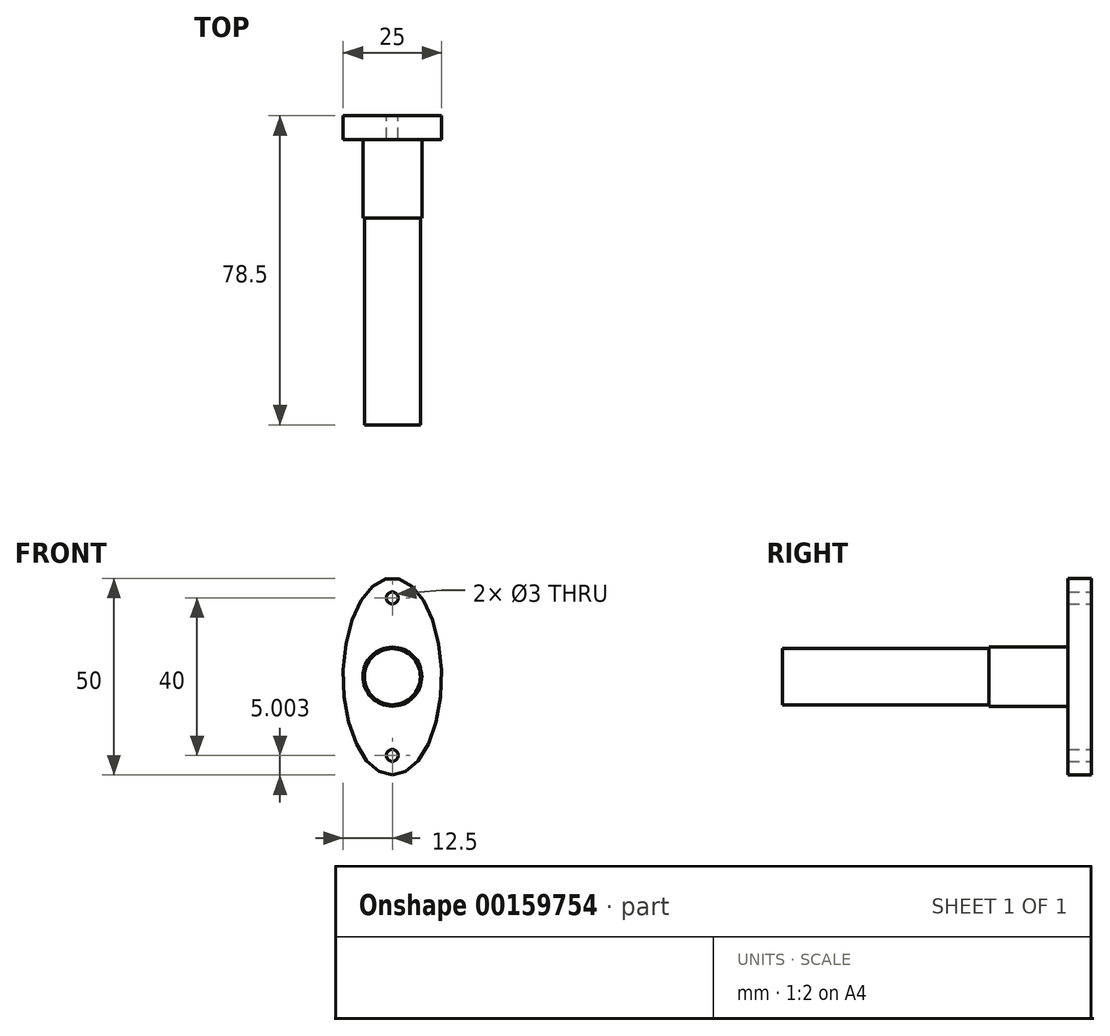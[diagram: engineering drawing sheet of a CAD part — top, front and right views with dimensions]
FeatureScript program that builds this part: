
annotation { "Feature Type Name" : "Feature", "Feature Type Description" : "" }
export const myFeature = defineFeature(function(context is Context, id is Id, definition is map)
    precondition{}
    {
        {
            var Q0;
            Q0=qCreatedBy(makeId("Front.planeOp"),FACE);
            var sketch = newSketch(context, id + "F0", { "sketchPlane" : qUnion([Q0])});
            skCircle(sketch, "E0", {"center": v(34.65, 46.32) * mm, "radius": 1.5 * mm});
            skCircle(sketch, "E1", {"center": v(34.65, 6.32) * mm, "radius": 1.5 * mm});
            skEllipse(sketch, "E2", {"center": v(34.65, 26.32) * mm, "majorRadius": 25 * mm, "minorRadius": 12.5 * mm, "majorAxis": v(0, -1)});
            skSolve(sketch);
        }
        {
            var Q0;
            Q0=makeQuery(id+"F0.imprint","IMPRINT",FACE,{"disambiguationData":[TD([[makeQuery(id+"F0.imprint","IMPRINT",EDGE,{"derivedFrom":sQuery(id+"F0.wireOp",EDGE,"E0")}),-1.0]])]});
            extrude(context, id + "F1", {"entities" : qUnion([Q0]), "depth" : 6 * mm});
        }
        {
            var Q0;
            Q0=makeQuery(id+"F1.opExtrude","CAP_FACE",FACE,{"disambiguationData":[OSD([sQuery(id+"F0.wireOp",EDGE,"E0"),sQuery(id+"F0.wireOp",EDGE,"E1"),sQuery(id+"F0.wireOp",EDGE,"E2")])],"isStart":false});
            var sketch = newSketch(context, id + "F2", { "sketchPlane" : qUnion([Q0])});
            skCircle(sketch, "E3", {"center": v(34.65, 26.32) * mm, "radius": 7.5 * mm});
            skSolve(sketch);
        }
        {
            var Q0;
            Q0=makeQuery(id+"F2.imprint","IMPRINT",FACE,{"disambiguationData":[TD([[makeQuery(id+"F2.imprint","IMPRINT",EDGE,{"derivedFrom":sQuery(id+"F2.wireOp",EDGE,"E3")}),1.0]])]});
            var Q1;
            Q1=sQuery(id+"F2.wireOp",EDGE,"E3");
            extrude(context, id + "F3", {"entities" : qUnion([Q0]), "operationType" : NewBodyOperationType.ADD, "surfaceEntities" : qUnion([Q1]), "depth" : 20 * mm});
        }
        {
            var Q0;
            Q0=makeQuery(id+"F3.opExtrude","CAP_FACE",FACE,{"disambiguationData":[OSD([sQuery(id+"F2.wireOp",EDGE,"E3")])],"isStart":false});
            var sketch = newSketch(context, id + "F4", { "sketchPlane" : qUnion([Q0])});
            skCircle(sketch, "E4", {"center": v(34.65, 26.32) * mm, "radius": 7.12 * mm});
            skSolve(sketch);
        }
        {
            var Q0;
            Q0=makeQuery(id+"F4.imprint","IMPRINT",FACE,{"disambiguationData":[TD([[makeQuery(id+"F4.imprint","IMPRINT",EDGE,{"derivedFrom":sQuery(id+"F4.wireOp",EDGE,"E4")}),1.0]])]});
            extrude(context, id + "F5", {"entities" : qUnion([Q0]), "operationType" : NewBodyOperationType.ADD, "depth" : 52.5 * mm});
        }
    });
